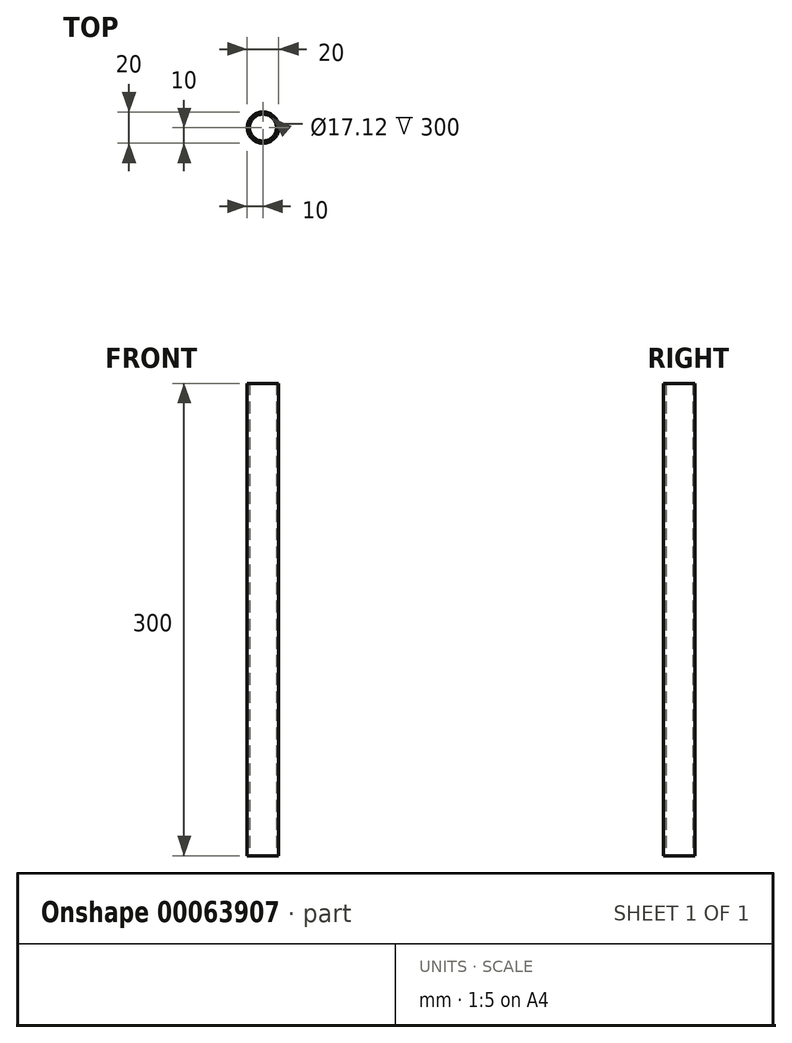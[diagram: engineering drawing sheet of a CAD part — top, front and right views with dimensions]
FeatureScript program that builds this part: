
annotation { "Feature Type Name" : "Feature", "Feature Type Description" : "" }
export const myFeature = defineFeature(function(context is Context, id is Id, definition is map)
    precondition{}
    {
        {
            var Q0;
            Q0=qCreatedBy(makeId("Top.planeOp"),FACE);
            var sketch = newSketch(context, id + "F0", { "sketchPlane" : qUnion([Q0])});
            skCircle(sketch, "E0", {"center": v(0, 0) * mm, "radius": 10 * mm});
            skCircle(sketch, "E1", {"center": v(0, 0) * mm, "radius": 8.56 * mm});
            skSolve(sketch);
        }
        {
            var Q0;
            Q0=makeQuery(id+"F0.imprint","IMPRINT",FACE,{"disambiguationData":[TD([[makeQuery(id+"F0.imprint","IMPRINT",EDGE,{"derivedFrom":sQuery(id+"F0.wireOp",EDGE,"E0")}),1.0]])]});
            extrude(context, id + "F1", {"entities" : qUnion([Q0]), "depth" : 300 * mm});
        }
    });
